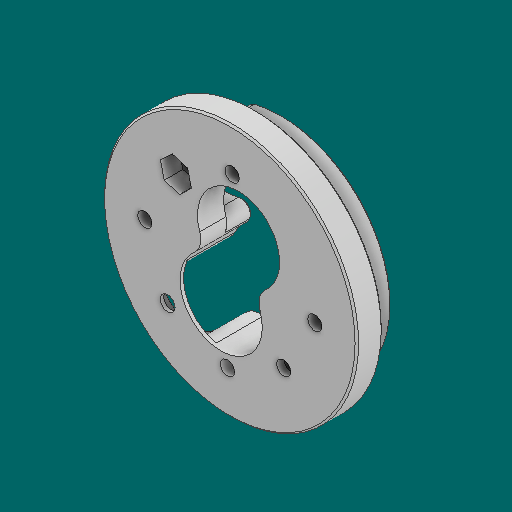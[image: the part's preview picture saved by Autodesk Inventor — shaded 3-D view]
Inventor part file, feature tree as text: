
AUTODESK INVENTOR PART (.ipt)
format: ipt  version: 2023.1 (Build 271208000, 208)  size: 693,760 bytes
history: native  units: in
note: dims shown in document units (in); Inventor stores cm internally (conversion verified against a paired STEP export)
features: extrude x6, sketch x4, projected_geometry x4, other x3, chamfer x2, fillet x2, reference x2
ambient origin geometry x8: Origin, YZ Plane, XZ Plane, XY Plane, X Axis, Y Axis, Z Axis, Center Point
bodies: Solid1 (feature_tree)
feature tree (23):
  extrude  "Extrusion1"  Depth=0.9in
  extrude  "Extrusion2"  Depth=0.35in
  chamfer  "Chamfer1"  Distance=0.35in
  fillet  "Fillet1"  Radius=3.4in
  extrude  "Extrusion3"  Depth=0.35in
  extrude  "Extrusion4"  Depth=0.25in
  extrude  "Extrusion5"  Depth=0.125in
  extrude  "Extrusion6"  Depth=0.1in TaperAngle=0.0deg
  fillet  "Fillet2"  Radius=0.33in
  chamfer  "Chamfer2"  Distance=0.1in
  sketch  "Sketch1"  dims[d0=1.1in d1=0.9in]
  reference  "Reference1"
  projected_geometry  "Projected Loop1"
  sketch  "Sketch3"  dims[d2=0.0098in d3=2.95in d4=0.35in d5=0.0in d6=3.4in]
  projected_geometry  "Projected Loop2"
  reference  "Reference2"
  sketch  "Sketch5"  dims[d7=0.35in d8=0.0in d11=0.19in]
  projected_geometry  "Projected Loop3"
  sketch  "Sketch6"  dims[d12=0.0236in d13=0.125in d14=45.0deg d15=0.25in d16=0.19in d17=0.1in d18=0.0in d19=0.33in d20=0.1in d21=0.0in d22=0.375in d23=0.19in d24=0.1in d25=0.0in d26=0.0472in d27=0.0in d28=0.125in d29=0.2in d30=0.0236in d31=0.125in d32=45.0deg d9=0.5in d10=0.0344in]
  projected_geometry  "Projected Loop4"
  other  "<userpath>\Documents\CAD\guardSwerve5\MainAssy.iam"
  other  "MainAssy.iam"
  other  "SteeringCoupler:1"
